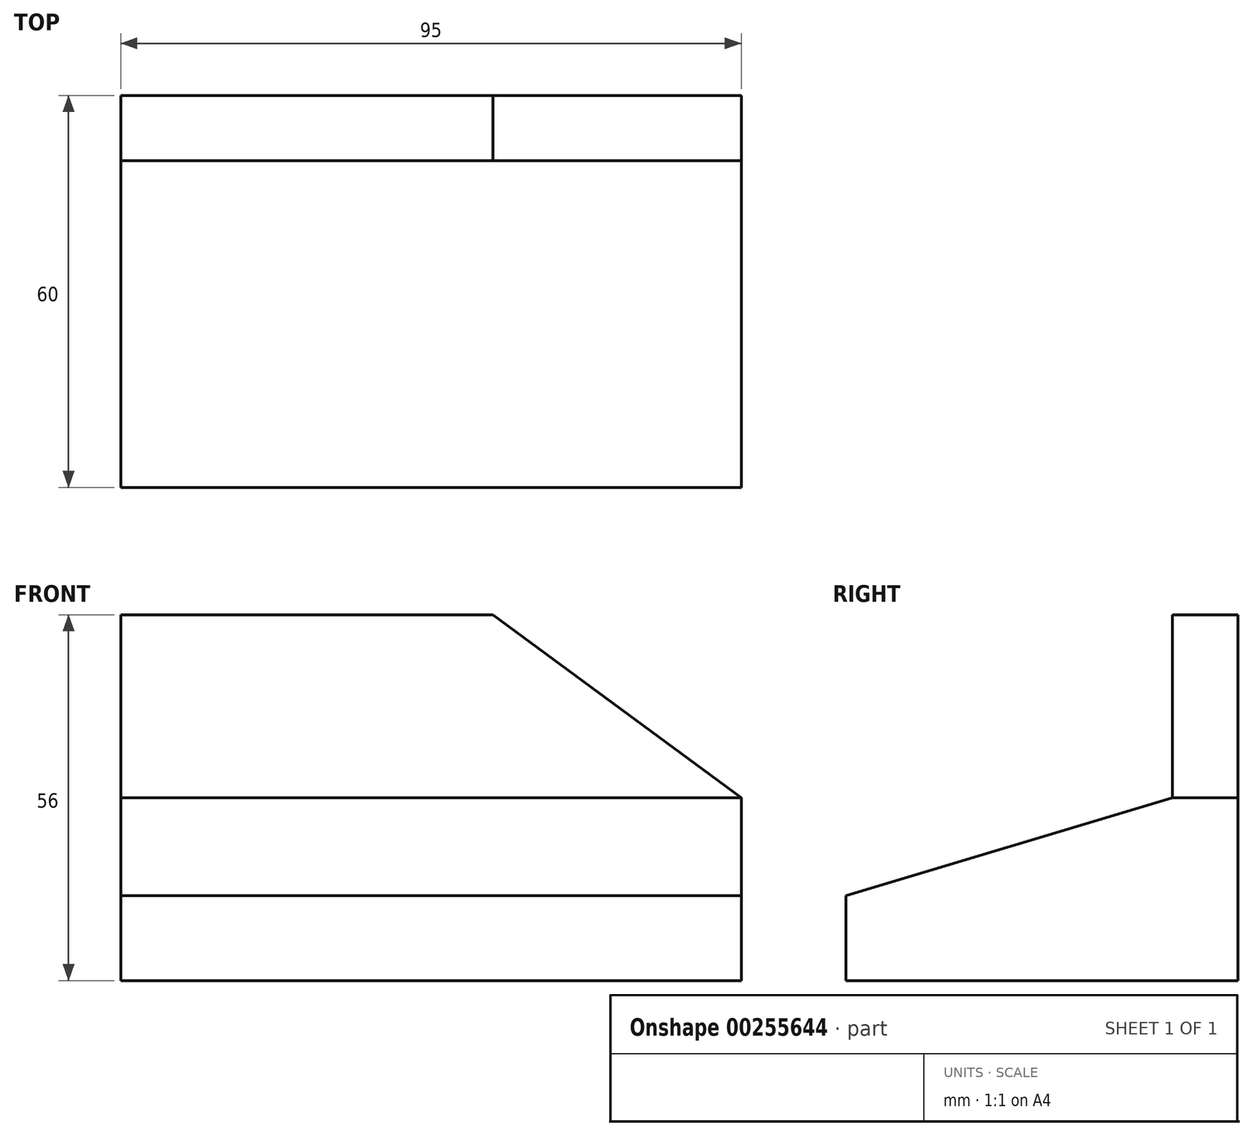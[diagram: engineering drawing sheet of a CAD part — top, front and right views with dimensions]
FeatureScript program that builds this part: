
annotation { "Feature Type Name" : "Feature", "Feature Type Description" : "" }
export const myFeature = defineFeature(function(context is Context, id is Id, definition is map)
    precondition{}
    {
        {
            var Q0;
            Q0=qCreatedBy(makeId("Right.planeOp"),FACE);
            var sketch = newSketch(context, id + "F0", { "sketchPlane" : qUnion([Q0])});
            skLineSegment(sketch, "E0", {"start": v(0, 0) * mm, "end": v(0, 56) * mm});
            skLineSegment(sketch, "E1", {"start": v(0, 56) * mm, "end": v(-10, 56) * mm});
            skLineSegment(sketch, "E2", {"start": v(-10, 56) * mm, "end": v(-10, 28) * mm});
            skLineSegment(sketch, "E3", {"start": v(-10, 28) * mm, "end": v(-60, 13) * mm});
            skLineSegment(sketch, "E4", {"start": v(-60, 13) * mm, "end": v(-60, 0) * mm});
            skLineSegment(sketch, "E5", {"start": v(-60, 0) * mm, "end": v(0, 0) * mm});
            skSolve(sketch);
        }
        {
            var Q0;
            Q0 = qSketchRegion(id + "F0", true);
            extrude(context, id + "F1", {"entities" : qUnion([Q0]), "depth" : 95 * mm});
        }
        {
            var Q0;
            Q0=makeQuery(id+"F1.opExtrude","SWEPT_FACE",FACE,{"disambiguationData":[OSD([sQuery(id+"F0.wireOp",EDGE,"E2")])]});
            var sketch = newSketch(context, id + "F2", { "sketchPlane" : qUnion([Q0])});
            skLineSegment(sketch, "E6", {"start": v(57, 56) * mm, "end": v(95, 28) * mm});
            skSolve(sketch);
        }
        {
            var Q0;
            {var subQ0=sQuery(id+"F2.wireOp",EDGE,"E6");Q0=makeQuery(id+"F2.imprint","IMPRINT",FACE,{"disambiguationData":[TD([[makeQuery(id+"F2.imprint","IMPRINT",EDGE,{"derivedFrom":subQ0}),1.0]])]});}
            extrude(context, id + "F3", {"entities" : qUnion([Q0]), "operationType" : NewBodyOperationType.REMOVE, "oppositeDirection" : true, "depth" : 25 * mm});
        }
    });
